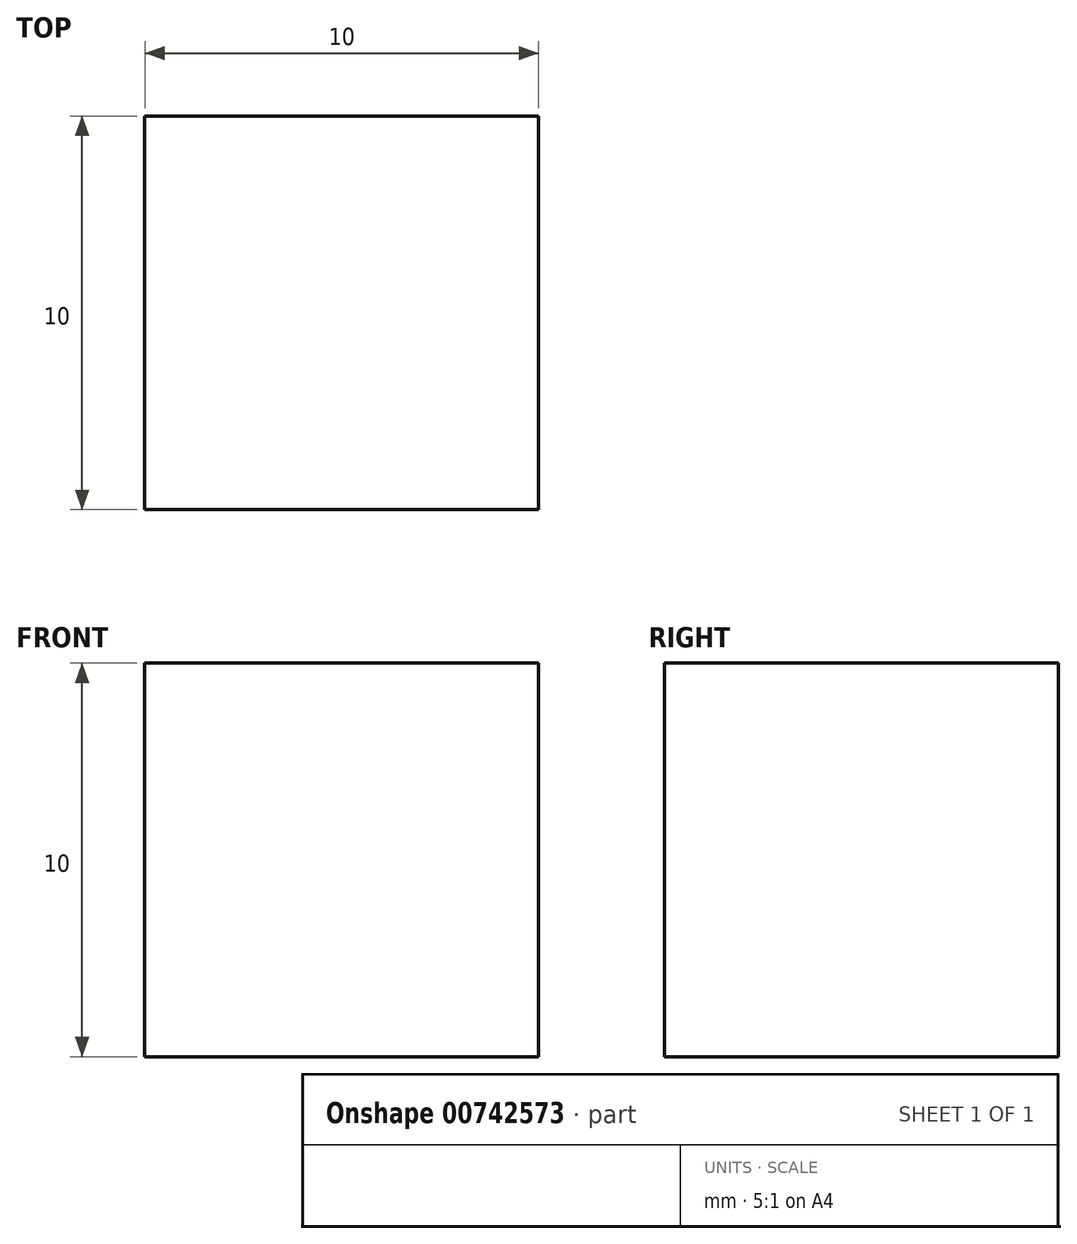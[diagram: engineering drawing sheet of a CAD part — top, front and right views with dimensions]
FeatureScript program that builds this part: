
annotation { "Feature Type Name" : "Feature", "Feature Type Description" : "" }
export const myFeature = defineFeature(function(context is Context, id is Id, definition is map)
    precondition{}
    {
        {
            var Q0;
            Q0=qCreatedBy(makeId("Top.planeOp"),FACE);
            var sketch = newSketch(context, id + "F0", { "sketchPlane" : qUnion([Q0])});
            skLineSegment(sketch, "E0.bottom", {"start": v(-11.37, 3.68) * mm, "end": v(-1.37, 3.68) * mm});
            skLineSegment(sketch, "E0.top", {"start": v(-11.37, -6.32) * mm, "end": v(-1.37, -6.32) * mm});
            skLineSegment(sketch, "E0.left", {"start": v(-11.37, 3.68) * mm, "end": v(-11.37, -6.32) * mm});
            skLineSegment(sketch, "E0.right", {"start": v(-1.37, 3.68) * mm, "end": v(-1.37, -6.32) * mm});
            skSolve(sketch);
        }
        {
            var Q0;
            Q0 = qSketchRegion(id + "F0", true);
            extrude(context, id + "F1", {"entities" : qUnion([Q0]), "depth" : 10 * mm, "offsetDistance" : 25 * mm});
        }
    });
